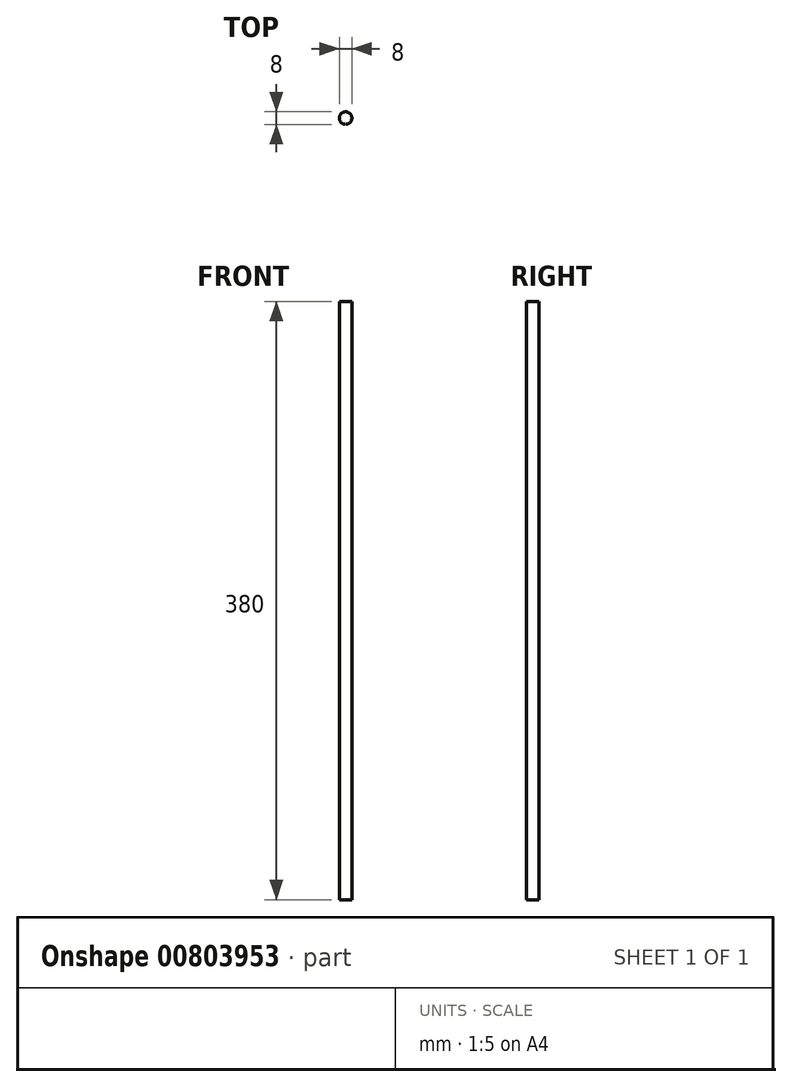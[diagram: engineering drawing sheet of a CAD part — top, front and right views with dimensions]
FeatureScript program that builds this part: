
annotation { "Feature Type Name" : "Feature", "Feature Type Description" : "" }
export const myFeature = defineFeature(function(context is Context, id is Id, definition is map)
    precondition{}
    {
        {
            var Q0;
            Q0=qCreatedBy(makeId("Top.planeOp"),FACE);
            var sketch = newSketch(context, id + "F0", { "sketchPlane" : qUnion([Q0])});
            skCircle(sketch, "E0", {"center": v(0, 0) * mm, "radius": 4 * mm});
            skSolve(sketch);
        }
        {
            var Q0;
            Q0=makeQuery(id+"F0.imprint","IMPRINT",FACE,{"disambiguationData":[TD([[makeQuery(id+"F0.imprint","IMPRINT",EDGE,{"derivedFrom":sQuery(id+"F0.wireOp",EDGE,"E0")}),1.0]])]});
            extrude(context, id + "F1", {"entities" : qUnion([Q0]), "depth" : 380 * mm, "offsetDistance" : 25 * mm});
        }
    });
